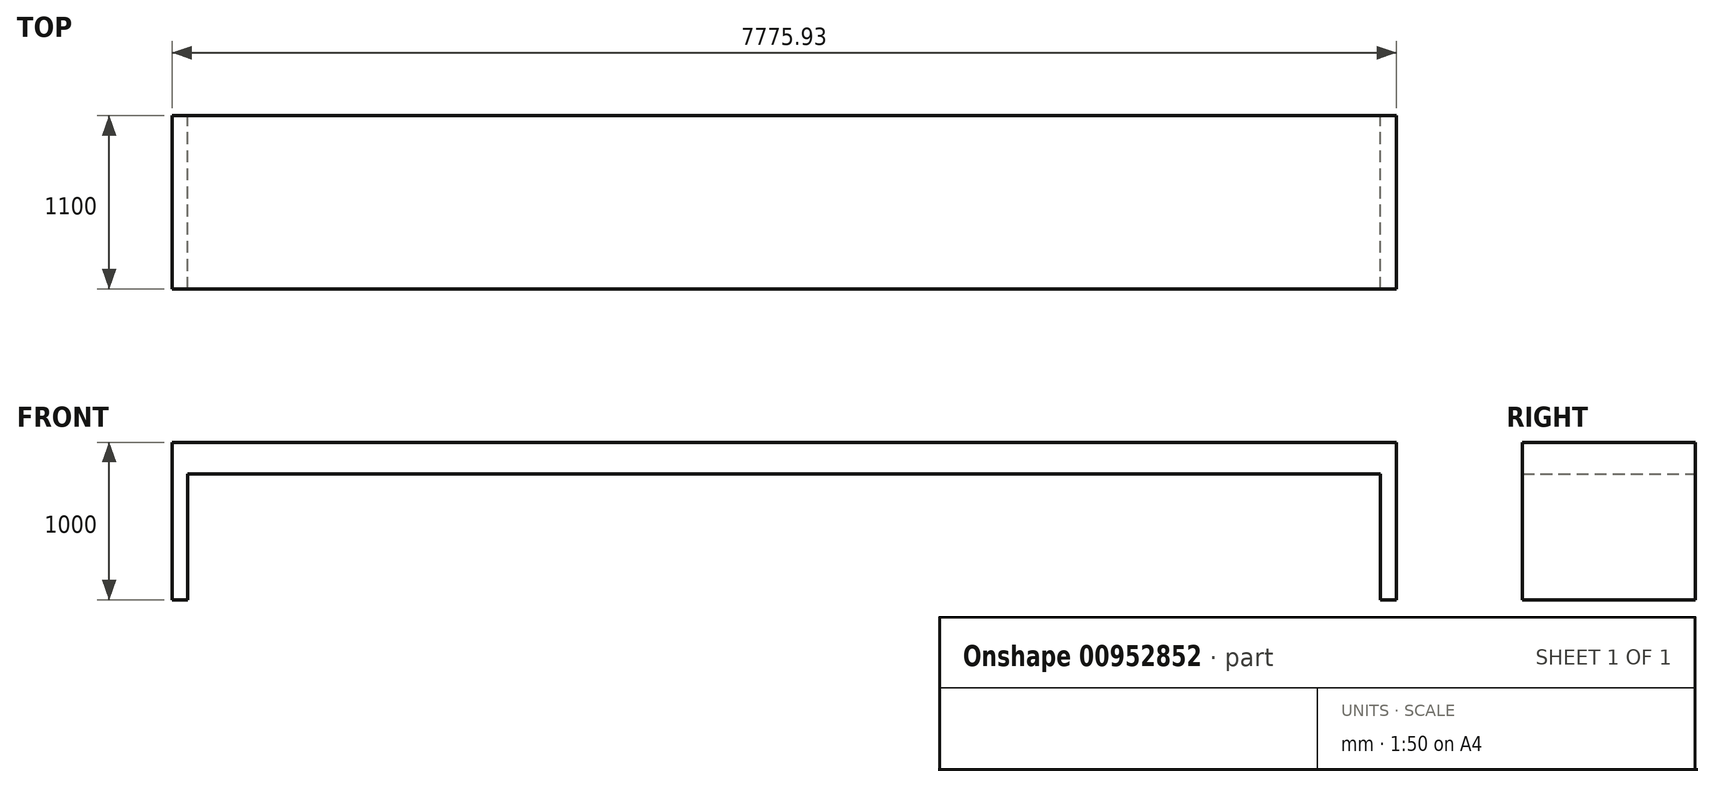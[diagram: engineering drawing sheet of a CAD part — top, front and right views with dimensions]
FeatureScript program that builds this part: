
annotation { "Feature Type Name" : "Feature", "Feature Type Description" : "" }
export const myFeature = defineFeature(function(context is Context, id is Id, definition is map)
    precondition{}
    {
        {
            var Q0;
            Q0=qCreatedBy(makeId("Front.planeOp"),FACE);
            var sketch = newSketch(context, id + "F0", { "sketchPlane" : qUnion([Q0])});
            skLineSegment(sketch, "E0", {"start": v(0, 0) * mm, "end": v(0, 800) * mm});
            skLineSegment(sketch, "E1", {"start": v(0, 800) * mm, "end": v(100, 800) * mm});
            skLineSegment(sketch, "E2", {"start": v(100, 800) * mm, "end": v(100, 0) * mm});
            skLineSegment(sketch, "E3", {"start": v(100, 0) * mm, "end": v(0, 0) * mm});
            skLineSegment(sketch, "E4", {"start": v(0, 800) * mm, "end": v(0, 1000) * mm});
            skLineSegment(sketch, "E5", {"start": v(0, 1000) * mm, "end": v(7775.93, 1000) * mm});
            skLineSegment(sketch, "E6", {"start": v(7775.93, 1000) * mm, "end": v(7775.93, 800) * mm});
            skLineSegment(sketch, "E7", {"start": v(7775.93, 800) * mm, "end": v(100, 800) * mm});
            skLineSegment(sketch, "E8", {"start": v(7775.93, 800) * mm, "end": v(7775.93, 0) * mm});
            skLineSegment(sketch, "E9", {"start": v(7775.93, 0) * mm, "end": v(7675.93, 0) * mm});
            skLineSegment(sketch, "E10", {"start": v(7675.93, 0) * mm, "end": v(7675.93, 800) * mm});
            skSolve(sketch);
        }
        {
            var Q0;
            Q0 = qSketchRegion(id + "F0", true);
            extrude(context, id + "F1", {"entities" : qUnion([Q0]), "depth" : 1100 * mm, "offsetDistance" : 25 * mm});
        }
    });
